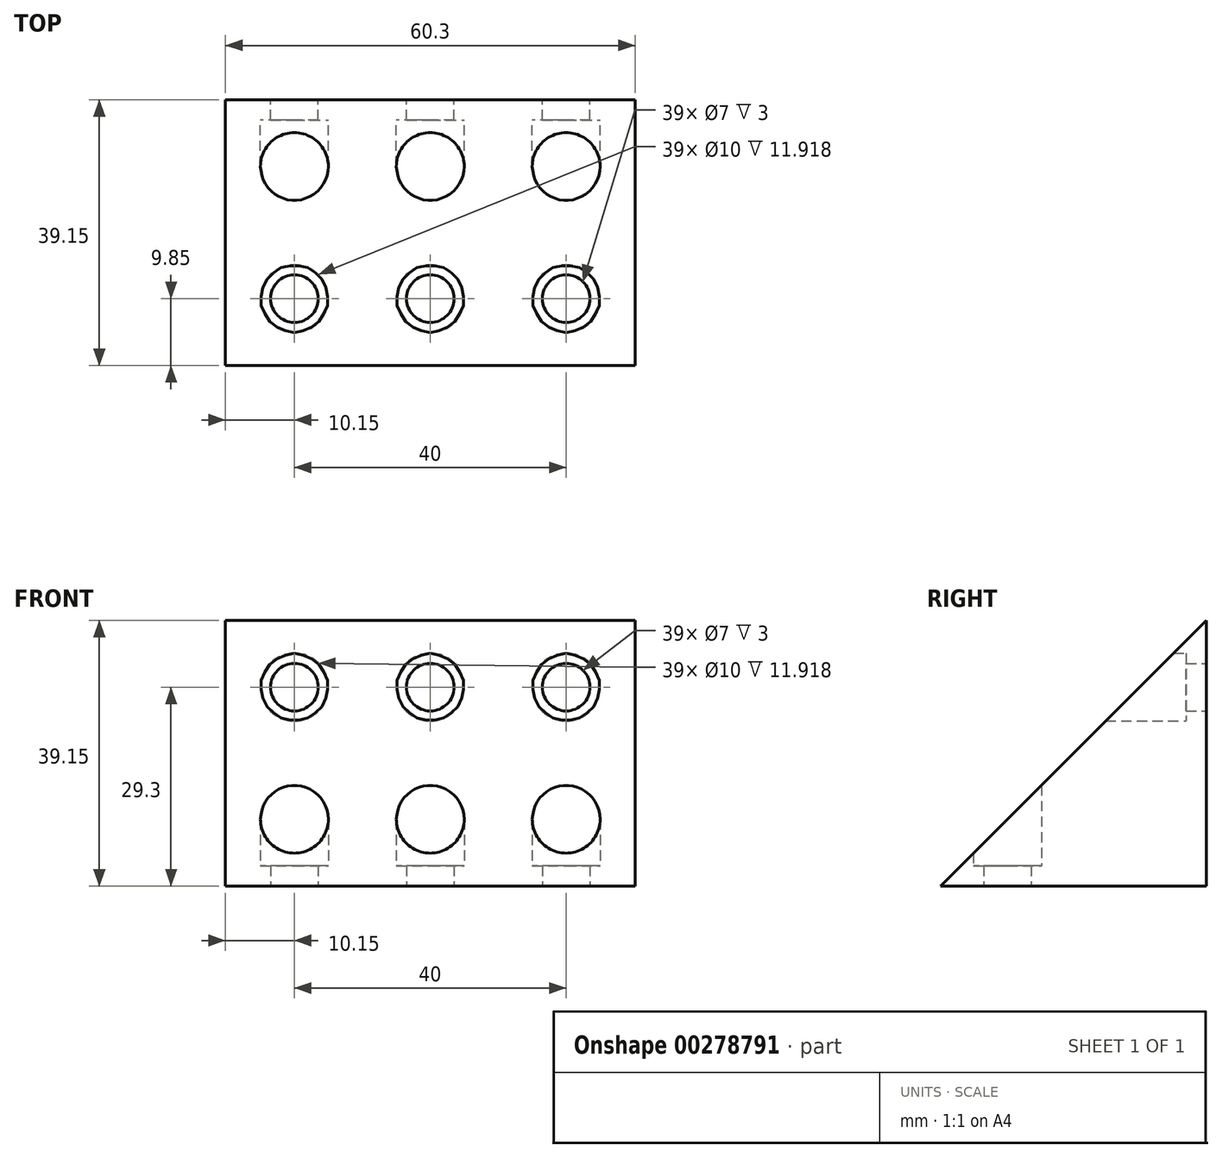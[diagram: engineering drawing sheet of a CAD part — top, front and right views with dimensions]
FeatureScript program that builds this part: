
annotation { "Feature Type Name" : "Feature", "Feature Type Description" : "" }
export const myFeature = defineFeature(function(context is Context, id is Id, definition is map)
    precondition{}
    {
        {
            var Q0;
            Q0=qCreatedBy(makeId("Right.planeOp"),FACE);
            var sketch = newSketch(context, id + "F0", { "sketchPlane" : qUnion([Q0])});
            skLineSegment(sketch, "E0", {"start": v(0, 0) * mm, "end": v(0, 39.15) * mm});
            skLineSegment(sketch, "E1", {"start": v(0, 0) * mm, "end": v(-39.15, 0) * mm});
            skLineSegment(sketch, "E2", {"start": v(-39.15, 0) * mm, "end": v(0, 39.15) * mm});
            skSolve(sketch);
        }
        {
            var Q0;
            Q0=makeQuery(id+"F0.imprint","IMPRINT",FACE,{"disambiguationData":[TD([[makeQuery(id+"F0.imprint","IMPRINT",EDGE,{"derivedFrom":sQuery(id+"F0.wireOp",EDGE,"E0")}),1.0]])]});
            extrude(context, id + "F1", {"entities" : qUnion([Q0]), "depth" : 30.15 * mm, "hasSecondDirection" : true, "secondDirectionOppositeDirection" : true, "secondDirectionDepth" : 30.15 * mm});
        }
        {
            var Q0;
            Q0=qCreatedBy(makeId("Front.planeOp"),FACE);
            var sketch = newSketch(context, id + "F2", { "sketchPlane" : qUnion([Q0])});
            skCircle(sketch, "E3", {"center": v(0, 29.3) * mm, "radius": 3.5 * mm});
            skCircle(sketch, "E4", {"center": v(-20, 29.3) * mm, "radius": 3.5 * mm});
            skCircle(sketch, "E5", {"center": v(20, 29.3) * mm, "radius": 3.5 * mm});
            skCircle(sketch, "E6", {"center": v(-20, 29.3) * mm, "radius": 5 * mm});
            skCircle(sketch, "E7", {"center": v(0, 29.3) * mm, "radius": 5 * mm});
            skCircle(sketch, "E8", {"center": v(20, 29.3) * mm, "radius": 5 * mm});
            skSolve(sketch);
        }
        {
            var Q0;
            Q0=makeQuery(id+"F2.imprint","IMPRINT",FACE,{"disambiguationData":[TD([[makeQuery(id+"F2.imprint","IMPRINT",EDGE,{"derivedFrom":sQuery(id+"F2.wireOp",EDGE,"E4")}),1.0]])]});
            var Q1;
            Q1=makeQuery(id+"F2.imprint","IMPRINT",FACE,{"disambiguationData":[TD([[makeQuery(id+"F2.imprint","IMPRINT",EDGE,{"derivedFrom":sQuery(id+"F2.wireOp",EDGE,"E3")}),1.0]])]});
            var Q2;
            Q2=makeQuery(id+"F2.imprint","IMPRINT",FACE,{"disambiguationData":[TD([[makeQuery(id+"F2.imprint","IMPRINT",EDGE,{"derivedFrom":sQuery(id+"F2.wireOp",EDGE,"E5")}),1.0]])]});
            extrude(context, id + "F3", {"entities" : qUnion([Q0, Q1, Q2]), "operationType" : NewBodyOperationType.REMOVE, "depth" : 25 * mm});
        }
        {
            var Q0;
            Q0=makeQuery(id+"F2.imprint","IMPRINT",FACE,{"disambiguationData":[TD([[makeQuery(id+"F2.imprint","IMPRINT",EDGE,{"derivedFrom":sQuery(id+"F2.wireOp",EDGE,"E5")}),-1.0]])]});
            var Q1;
            Q1=makeQuery(id+"F2.imprint","IMPRINT",FACE,{"disambiguationData":[TD([[makeQuery(id+"F2.imprint","IMPRINT",EDGE,{"derivedFrom":sQuery(id+"F2.wireOp",EDGE,"E3")}),-1.0]])]});
            var Q2;
            Q2=makeQuery(id+"F2.imprint","IMPRINT",FACE,{"disambiguationData":[TD([[makeQuery(id+"F2.imprint","IMPRINT",EDGE,{"derivedFrom":sQuery(id+"F2.wireOp",EDGE,"E4")}),-1.0]])]});
            extrude(context, id + "F4", {"entities" : qUnion([Q0, Q1, Q2]), "operationType" : NewBodyOperationType.REMOVE, "depth" : 25 * mm, "hasSecondDirection" : true, "secondDirectionOppositeDirection" : false, "secondDirectionDepth" : 3 * mm});
        }
        {
            var Q0;
            Q0=qCreatedBy(makeId("Top.planeOp"),FACE);
            var sketch = newSketch(context, id + "F5", { "sketchPlane" : qUnion([Q0])});
            skCircle(sketch, "E9", {"center": v(-20, -29.3) * mm, "radius": 3.5 * mm});
            skCircle(sketch, "E10", {"center": v(0, -29.3) * mm, "radius": 3.5 * mm});
            skCircle(sketch, "E11", {"center": v(20, -29.3) * mm, "radius": 3.5 * mm});
            skCircle(sketch, "E12", {"center": v(-20, -29.3) * mm, "radius": 5 * mm});
            skCircle(sketch, "E13", {"center": v(0, -29.3) * mm, "radius": 5 * mm});
            skCircle(sketch, "E14", {"center": v(20, -29.3) * mm, "radius": 5 * mm});
            skSolve(sketch);
        }
        {
            var Q0;
            Q0=makeQuery(id+"F5.imprint","IMPRINT",FACE,{"disambiguationData":[TD([[makeQuery(id+"F5.imprint","IMPRINT",EDGE,{"derivedFrom":sQuery(id+"F5.wireOp",EDGE,"E11")}),1.0]])]});
            var Q1;
            Q1=makeQuery(id+"F5.imprint","IMPRINT",FACE,{"disambiguationData":[TD([[makeQuery(id+"F5.imprint","IMPRINT",EDGE,{"derivedFrom":sQuery(id+"F5.wireOp",EDGE,"E10")}),1.0]])]});
            var Q2;
            Q2=makeQuery(id+"F5.imprint","IMPRINT",FACE,{"disambiguationData":[TD([[makeQuery(id+"F5.imprint","IMPRINT",EDGE,{"derivedFrom":sQuery(id+"F5.wireOp",EDGE,"E9")}),1.0]])]});
            extrude(context, id + "F6", {"entities" : qUnion([Q0, Q1, Q2]), "operationType" : NewBodyOperationType.REMOVE, "depth" : 25 * mm});
        }
        {
            var Q0;
            Q0=makeQuery(id+"F5.imprint","IMPRINT",FACE,{"disambiguationData":[TD([[makeQuery(id+"F5.imprint","IMPRINT",EDGE,{"derivedFrom":sQuery(id+"F5.wireOp",EDGE,"E9")}),-1.0]])]});
            var Q1;
            Q1=makeQuery(id+"F5.imprint","IMPRINT",FACE,{"disambiguationData":[TD([[makeQuery(id+"F5.imprint","IMPRINT",EDGE,{"derivedFrom":sQuery(id+"F5.wireOp",EDGE,"E10")}),-1.0]])]});
            var Q2;
            Q2=makeQuery(id+"F5.imprint","IMPRINT",FACE,{"disambiguationData":[TD([[makeQuery(id+"F5.imprint","IMPRINT",EDGE,{"derivedFrom":sQuery(id+"F5.wireOp",EDGE,"E11")}),-1.0]])]});
            extrude(context, id + "F7", {"entities" : qUnion([Q0, Q1, Q2]), "operationType" : NewBodyOperationType.REMOVE, "depth" : 25 * mm, "hasSecondDirection" : true, "secondDirectionOppositeDirection" : false, "secondDirectionDepth" : 3 * mm});
        }
    });
